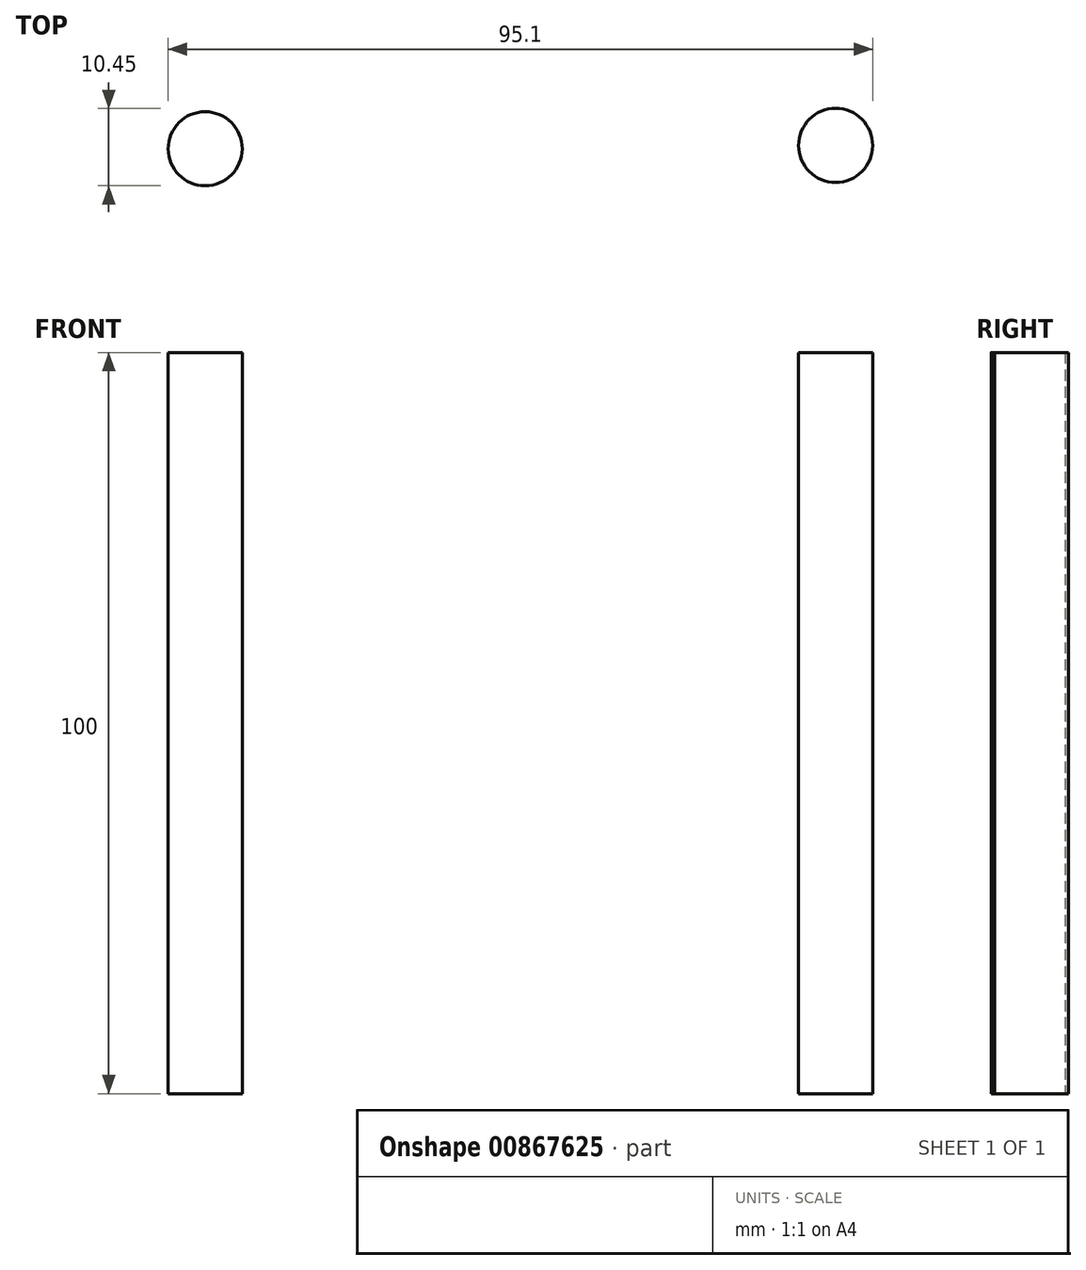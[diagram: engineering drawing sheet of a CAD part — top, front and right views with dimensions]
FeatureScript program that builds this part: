
annotation { "Feature Type Name" : "Feature", "Feature Type Description" : "" }
export const myFeature = defineFeature(function(context is Context, id is Id, definition is map)
    precondition{}
    {
        {
            var Q0;
            Q0=qCreatedBy(makeId("Top.planeOp"),FACE);
            var sketch = newSketch(context, id + "F0", { "sketchPlane" : qUnion([Q0])});
            skCircle(sketch, "E0", {"center": v(-53.98, 0) * mm, "radius": 5 * mm});
            skCircle(sketch, "E1", {"center": v(31.12, 0.45) * mm, "radius": 5 * mm});
            skSolve(sketch);
        }
        {
            var Q0;
            Q0=makeQuery(id+"F0.imprint","IMPRINT",FACE,{"disambiguationData":[TD([[makeQuery(id+"F0.imprint","IMPRINT",EDGE,{"derivedFrom":sQuery(id+"F0.wireOp",EDGE,"E0")}),1.0]])]});
            var Q1;
            Q1=makeQuery(id+"F0.imprint","IMPRINT",FACE,{"disambiguationData":[TD([[makeQuery(id+"F0.imprint","IMPRINT",EDGE,{"derivedFrom":sQuery(id+"F0.wireOp",EDGE,"E1")}),1.0]])]});
            extrude(context, id + "F1", {"entities" : qUnion([Q0, Q1]), "depth" : 100 * mm, "offsetDistance" : 25 * mm});
        }
    });
